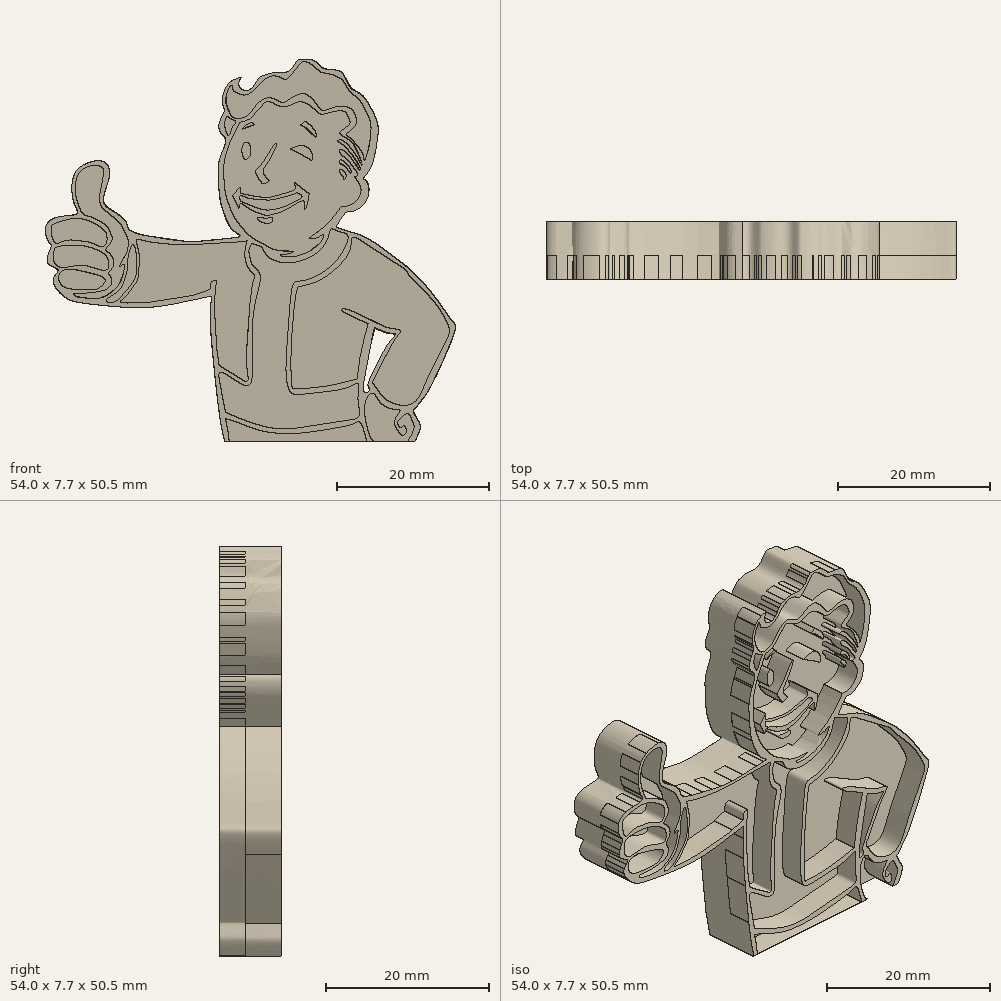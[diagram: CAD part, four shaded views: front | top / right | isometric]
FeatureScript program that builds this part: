
annotation { "Feature Type Name" : "Feature", "Feature Type Description" : "" }
export const myFeature = defineFeature(function(context is Context, id is Id, definition is map)
    precondition{}
    {
        {
            var Q0;
            Q0=qCreatedBy(makeId("Front.planeOp"),FACE);
            var sketch = newSketch(context, id + "F0", { "sketchPlane" : qUnion([Q0])});
            skPoint(sketch, "E0.middle", {"position": v(0.06, -0.1) * mm});
            skFitSpline(sketch, "E1", {"points": [v(-9.7, 22.56) * mm, v(-10.04, 21.79) * mm, v(-9.82, 21.14) * mm, v(-8.92, 20.8) * mm, v(-8.11, 21.32) * mm, v(-7.34, 22.43) * mm, v(-6.7, 22.81) * mm, v(-5.37, 23.16) * mm, v(-4.26, 23.16) * mm, v(-3.5, 23.33) * mm, v(-2.85, 23.97) * mm, v(-2.12, 24.87) * mm, v(-1.35, 24.95) * mm, v(-0.37, 24.87) * mm, v(0.57, 24.18) * mm, v(1.22, 23.71) * mm, v(3.01, 23.45) * mm, v(3.87, 22.73) * mm, v(4.77, 21.1) * mm, v(6, 20.37) * mm, v(7.3, 18.66) * mm, v(8.27, 16.35) * mm, v(8.19, 14.04) * mm, v(7.46, 10.84) * mm, v(6.38, 9.19) * mm], "startDerivative": vector(-13.84, -23.05) * mm, "endDerivative": vector(-23.15, -28.05) * mm});
            skFitSpline(sketch, "E2", {"points": [v(6.38, 9.19) * mm, v(7, 8.5) * mm, v(6.7, 6.13) * mm, v(4.94, 4.87) * mm, v(4.26, 4.8) * mm, v(2.75, 2.75) * mm], "startDerivative": vector(4.77, -3.33) * mm, "endDerivative": vector(-6.57, -11.06) * mm});
            skFitSpline(sketch, "E3", {"points": [v(2.75, 2.75) * mm, v(4.35, 2.21) * mm, v(6.38, 1.52) * mm, v(9.04, -0.1) * mm, v(11.12, -1.69) * mm, v(12.82, -3.08) * mm, v(14.78, -5.17) * mm, v(16.69, -7.65) * mm, v(18.02, -9.55) * mm, v(18.5, -10.25) * mm, v(17.75, -12.91) * mm], "startDerivative": vector(18.26, -6.4) * mm, "endDerivative": vector(-11.57, -29.08) * mm});
            skFitSpline(sketch, "E4", {"points": [v(17.75, -12.91) * mm, v(16.89, -14.9) * mm, v(14.98, -18.8) * mm, v(12.95, -21.49) * mm], "startDerivative": vector(-2.83, -6.5) * mm, "endDerivative": vector(-6.08, -7.14) * mm});
            skFitSpline(sketch, "E5", {"points": [v(12.95, -21.49) * mm, v(13.68, -22.87) * mm, v(13.9, -23.6) * mm, v(13.2, -25.5) * mm], "startDerivative": vector(2.25, -4.32) * mm, "endDerivative": vector(-2.57, -5.35) * mm});
            skLineSegment(sketch, "E6", {"start": v(13.2, -25.5) * mm, "end": v(6.78, -25.5) * mm});
            skFitSpline(sketch, "E7", {"points": [v(6.78, -25.5) * mm, v(6.33, -24.3) * mm, v(6.03, -23) * mm, v(6.15, -20.61) * mm, v(7.18, -18.83) * mm, v(7, -18.1) * mm, v(8, -15.77) * mm, v(9.55, -12.84) * mm, v(10.6, -11.37) * mm, v(9.94, -11.24) * mm, v(7.9, -10.53) * mm], "startDerivative": vector(-5.69, 14.05) * mm, "endDerivative": vector(-19.4, 8.58) * mm});
            skFitSpline(sketch, "E8", {"points": [v(7.9, -10.53) * mm, v(7.53, -12.15) * mm, v(6.78, -15.3) * mm, v(6.53, -19.02) * mm, v(7.18, -18.83) * mm], "startDerivative": vector(-1.55, -7.03) * mm, "endDerivative": vector(5.44, 3.45) * mm});
            skLineSegment(sketch, "E9", {"start": v(6.78, -25.5) * mm, "end": v(-11.9, -25.5) * mm});
            skFitSpline(sketch, "E10", {"points": [v(-11.9, -25.5) * mm, v(-12.56, -22.2) * mm, v(-13.1, -17.3) * mm, v(-13.7, -11.3) * mm, v(-13.67, -6.3) * mm], "startDerivative": vector(-3.46, 15) * mm, "endDerivative": vector(0.78, 19.03) * mm});
            skFitSpline(sketch, "E11", {"points": [v(-13.67, -6.3) * mm, v(-15.65, -6.7) * mm, v(-20.49, -7.64) * mm, v(-24.77, -7.77) * mm, v(-28.83, -7.42) * mm, v(-32.08, -6.87) * mm, v(-33.62, -5.84) * mm, v(-34.48, -4.05) * mm, v(-33.84, -2.9) * mm, v(-35.12, -2.03) * mm, v(-34.65, 0.4) * mm], "startDerivative": vector(-19.96, -3.7) * mm, "endDerivative": vector(14.11, 33.33) * mm});
            skFitSpline(sketch, "E12", {"points": [v(-34.65, 0.4) * mm, v(-35.3, 1.22) * mm, v(-35.38, 3.06) * mm, v(-33.92, 4.13) * mm, v(-31.65, 4.43) * mm, v(-31.27, 4.68) * mm, v(-31.65, 5.7) * mm, v(-32.04, 7.85) * mm, v(-31.44, 10.16) * mm, v(-29.39, 11.44) * mm, v(-27.63, 11.31) * mm, v(-27.03, 9.77) * mm, v(-27.55, 7.93) * mm, v(-27.8, 6) * mm, v(-26.78, 5.02) * mm, v(-24.94, 3.57) * mm, v(-24.42, 2.46) * mm, v(-20.45, 1.39) * mm, v(-15.82, 0.92) * mm, v(-10.82, 1.39) * mm, v(-9.75, 1.6) * mm, v(-10.82, 2.42) * mm, v(-12.1, 4.9) * mm, v(-12.53, 6.56) * mm, v(-12.74, 9.26) * mm, v(-12.53, 11.87) * mm, v(-11.76, 14.35) * mm, v(-12.49, 15.34) * mm, v(-12.53, 16.75) * mm, v(-11.93, 18.12) * mm, v(-12.15, 18.89) * mm, v(-12.1, 20.26) * mm, v(-11.18, 21.89) * mm, v(-9.7, 22.56) * mm], "startDerivative": vector(-31.91, 29.31) * mm, "endDerivative": vector(57.09, 16.2) * mm});
            skSolve(sketch);
        }
        {
            var Q0;
            Q0=makeQuery(id+"F0.imprint","IMPRINT",FACE,{"disambiguationData":[TD([[makeQuery(id+"F0.imprint","IMPRINT",EDGE,{"derivedFrom":sQuery(id+"F0.wireOp",EDGE,"E1")}),-1.0]])]});
            extrude(context, id + "F1", {"entities" : qUnion([Q0]), "depth" : 12.7 * mm});
        }
        {
            var Q0;
            Q0=makeQuery(id+"F1.opExtrude","CAP_FACE",FACE,{"disambiguationData":[OSD([sQuery(id+"F0.wireOp",EDGE,"E1"),sQuery(id+"F0.wireOp",EDGE,"E2"),sQuery(id+"F0.wireOp",EDGE,"E3"),sQuery(id+"F0.wireOp",EDGE,"E4"),sQuery(id+"F0.wireOp",EDGE,"E5"),sQuery(id+"F0.wireOp",EDGE,"E6"),sQuery(id+"F0.wireOp",EDGE,"E7"),sQuery(id+"F0.wireOp",EDGE,"E8"),sQuery(id+"F0.wireOp",EDGE,"E9"),sQuery(id+"F0.wireOp",EDGE,"E10"),sQuery(id+"F0.wireOp",EDGE,"E11"),sQuery(id+"F0.wireOp",EDGE,"E12")])],"isStart":false});
            var sketch = newSketch(context, id + "F2", { "sketchPlane" : qUnion([Q0])});
            skFitSpline(sketch, "E13", {"points": [v(-9.77, 1.56) * mm, v(-9.06, 1.13) * mm, v(-8.33, 0.7) * mm, v(-7.43, 0.36) * mm, v(-7.03, 0.19) * mm, v(-6.37, -0.92) * mm, v(-5.34, -1.57) * mm, v(-4, -1.89) * mm, v(-2.13, -1.72) * mm, v(-0.3, -0.99) * mm, v(0.9, 0) * mm, v(1.72, 1.36) * mm, v(2.2, 2.65) * mm, v(2.75, 2.75) * mm], "startDerivative": vector(11.12, -6.66) * mm, "endDerivative": vector(11.6, -0.98) * mm});
            skFitSpline(sketch, "E14", {"points": [v(-9.77, 1.56) * mm, v(-11.05, 2.67) * mm, v(-12.22, 5.26) * mm, v(-12.45, 6.12) * mm, v(-12.69, 8.2) * mm, v(-12.76, 10.65) * mm, v(-12.18, 12.77) * mm, v(-11.75, 14.25) * mm, v(-12.2, 14.99) * mm, v(-12.5, 15.37) * mm, v(-12.66, 15.93) * mm, v(-12.54, 16.72) * mm, v(-12, 17.84) * mm, v(-11.94, 18.27) * mm, v(-12.15, 18.91) * mm, v(-12.2, 19.7) * mm, v(-11.64, 21.33) * mm, v(-10.55, 22.27) * mm, v(-9.7, 22.56) * mm, v(-10.03, 21.83) * mm, v(-9.7, 21.03) * mm, v(-8.8, 20.82) * mm, v(-8.16, 21.26) * mm, v(-7.83, 21.71) * mm, v(-7.6, 22.08) * mm, v(-7.2, 22.56) * mm, v(-6.51, 22.88) * mm, v(-5.33, 23.16) * mm, v(-4.5, 23.16) * mm, v(-3.8, 23.2) * mm, v(-3.09, 23.66) * mm, v(-2.63, 24.3) * mm, v(-1.95, 24.93) * mm, v(-0.4, 24.88) * mm, v(0.39, 24.37) * mm, v(1.14, 23.74) * mm, v(2.32, 23.57) * mm, v(3.35, 23.31) * mm, v(3.96, 22.56) * mm, v(4.58, 21.32) * mm, v(5.66, 20.58) * mm, v(6.6, 19.76) * mm, v(7.4, 18.48) * mm, v(8.15, 16.84) * mm, v(8.33, 15.24) * mm, v(8.16, 13.82) * mm, v(8.02, 12.98) * mm, v(7.69, 11.5) * mm, v(7.2, 10.32) * mm, v(6.38, 9.19) * mm], "startDerivative": vector(-52.64, 32.33) * mm, "endDerivative": vector(-38.83, -49.05) * mm});
            skFitSpline(sketch, "E15", {"points": [v(6.38, 9.19) * mm, v(6.69, 8.95) * mm, v(7.05, 8.33) * mm, v(7.11, 7.93) * mm, v(7.12, 7.73) * mm, v(7.07, 7.12) * mm, v(7.03, 6.95) * mm, v(6.77, 6.23) * mm, v(6.26, 5.59) * mm, v(6.12, 5.46) * mm, v(5.4, 5) * mm, v(4.94, 4.87) * mm, v(4.65, 4.86) * mm, v(4.31, 4.82) * mm, v(3.95, 4.55) * mm, v(3.39, 3.8) * mm, v(2.75, 2.75) * mm], "startDerivative": vector(5.52, -3.35) * mm, "endDerivative": vector(-6.55, -11.06) * mm});
            skFitSpline(sketch, "E16", {"points": [v(-10.44, 17.13) * mm, v(-10.96, 17.45) * mm, v(-11.34, 18.04) * mm, v(-11.6, 18.7) * mm, v(-11.75, 19.8) * mm, v(-11.23, 21.23) * mm, v(-10.93, 21.52) * mm, v(-10.8, 20.94) * mm, v(-10.28, 20.5) * mm, v(-9.53, 20.24) * mm, v(-8.82, 20.3) * mm, v(-7.94, 20.85) * mm, v(-7.5, 21.35) * mm, v(-6.65, 22.2) * mm, v(-6.05, 22.56) * mm, v(-5.44, 22.74) * mm, v(-4.61, 22.56) * mm, v(-3.9, 22.25) * mm, v(-3.43, 22.56) * mm, v(-2.62, 23.44) * mm, v(-1.72, 24.54) * mm, v(-1.27, 24.6) * mm, v(-0.48, 24.27) * mm, v(0.44, 23.48) * mm, v(1.04, 23.15) * mm, v(2.28, 22.92) * mm, v(3.07, 22.56) * mm, v(3.66, 22.1) * mm, v(4.54, 20.76) * mm, v(5.26, 20.13) * mm, v(6.04, 19.32) * mm, v(7.03, 17.43) * mm, v(7.35, 16.35) * mm, v(7.37, 15.24) * mm, v(7.06, 13.08) * mm, v(6.52, 11.55) * mm, v(6.38, 12.2) * mm, v(5.59, 13.53) * mm, v(4.65, 14.54) * mm, v(4.17, 14.99) * mm, v(4.56, 15.37) * mm, v(5.44, 16.48) * mm, v(5.2, 17.85) * mm, v(4.9, 18.3) * mm, v(4.45, 18.58) * mm, v(3.54, 18.75) * mm, v(2.13, 18.46) * mm, v(1.07, 18.17) * mm, v(0.4, 18.73) * mm, v(-0.3, 19.66) * mm, v(-0.89, 20.13) * mm, v(-1.41, 20.38) * mm, v(-2.69, 20.06) * mm, v(-4.13, 19.23) * mm, v(-4.81, 19.41) * mm, v(-5.44, 19.74) * mm, v(-5.94, 19.86) * mm, v(-6.52, 19.74) * mm, v(-7.63, 18.96) * mm, v(-8.52, 17.81) * mm, v(-9.12, 17.34) * mm, v(-9.96, 17.07) * mm, v(-10.44, 17.13) * mm]});
            skFitSpline(sketch, "E17", {"points": [v(-11.5, 17.38) * mm, v(-11.18, 17.14) * mm, v(-10.42, 16.69) * mm, v(-10.6, 16.34) * mm, v(-10.95, 15.74) * mm, v(-11.33, 14.88) * mm, v(-11.76, 15.54) * mm, v(-11.89, 16.52) * mm, v(-11.6, 17.3) * mm, v(-11.5, 17.38) * mm]});
            skFitSpline(sketch, "E18", {"points": [v(-8.5, 17.07) * mm, v(-7.8, 17.84) * mm, v(-6.96, 18.76) * mm, v(-6.39, 19.32) * mm, v(-5.69, 19.25) * mm, v(-4.91, 18.85) * mm, v(-3.98, 18.69) * mm, v(-2.93, 18.98) * mm, v(-2.24, 19.3) * mm, v(-1.33, 19.22) * mm, v(0, 18.27) * mm, v(0.62, 17.74) * mm, v(1.37, 17.73) * mm, v(2.8, 18.1) * mm, v(3.93, 18) * mm, v(4.38, 17.34) * mm, v(4.55, 16.34) * mm, v(3.3, 15.25) * mm, v(4.32, 14.43) * mm, v(5.56, 12.92) * mm, v(6.2, 10.95) * mm, v(5.39, 12.34) * mm, v(3.93, 14.05) * mm, v(3.36, 14.33) * mm, v(2.98, 14.14) * mm], "startDerivative": vector(16.7, 18.66) * mm, "endDerivative": vector(-11.22, -13.2) * mm});
            skFitSpline(sketch, "E19", {"points": [v(2.98, 14.14) * mm, v(3.72, 13.62) * mm, v(4.72, 12.55) * mm, v(5.45, 11.57) * mm, v(5.94, 10.63) * mm, v(5.99, 10.22) * mm, v(5.7, 10.54) * mm, v(4.9, 11.76) * mm, v(3.63, 13) * mm, v(3.2, 13) * mm, v(3.42, 12.44) * mm, v(4.21, 11.76) * mm, v(5.13, 10.63) * mm, v(5.67, 9.66) * mm, v(5.22, 9.43) * mm], "startDerivative": vector(9.68, -6.14) * mm, "endDerivative": vector(-11.73, -2.82) * mm});
            skFitSpline(sketch, "E20", {"points": [v(5.22, 9.43) * mm, v(5.76, 8.62) * mm, v(6.07, 7.6) * mm, v(5.75, 6.58) * mm, v(5.22, 6.01) * mm, v(4.38, 5.6) * mm, v(3.5, 5.55) * mm], "startDerivative": vector(3.4, -4.56) * mm, "endDerivative": vector(-5.47, 0.19) * mm});
            skFitSpline(sketch, "E21", {"points": [v(3.5, 5.55) * mm, v(2.9, 4.68) * mm, v(1.92, 3.52) * mm, v(0.36, 2.12) * mm, v(-0.7, 1.32) * mm, v(-0.2, 1.3) * mm, v(0.69, 1.58) * mm, v(1.13, 1.83) * mm, v(1.07, 1.33) * mm, v(0.42, 0.41) * mm, v(-1.03, -0.55) * mm, v(-2.99, -1.09) * mm, v(-4.45, -0.97) * mm, v(-4.49, -0.82) * mm, v(-3.93, -0.78) * mm, v(-2.92, -0.53) * mm, v(-2.66, -0.36) * mm, v(-3.4, -0.36) * mm, v(-5.37, -0.13) * mm, v(-6.38, 0.36) * mm, v(-7.95, 1.2) * mm, v(-9.16, 2.22) * mm, v(-10.72, 4.3) * mm, v(-11.38, 5.87) * mm, v(-11.8, 7.24) * mm, v(-12.02, 10.53) * mm, v(-11.81, 12.04) * mm, v(-11.11, 14.11) * mm, v(-10.46, 15.38) * mm, v(-9.9, 16.53) * mm, v(-9.36, 16.74) * mm, v(-8.5, 17.07) * mm], "startDerivative": vector(-18.48, -28.57) * mm, "endDerivative": vector(32.44, 14.04) * mm});
            skLineSegment(sketch, "E22", {"start": v(-1.89, 16.24) * mm, "end": v(-1.29, 16.73) * mm});
            skPoint(sketch, "E23.4.internal.orphan", {"position": v(0, 14.81) * mm});
            skFitSpline(sketch, "E24", {"points": [v(-1.89, 16.24) * mm, v(-1.57, 16.1) * mm, v(-0.73, 15.53) * mm, v(0.17, 14.6) * mm, v(0.22, 14.89) * mm, v(-0.1, 15.63) * mm, v(-0.81, 16.42) * mm, v(-1.29, 16.73) * mm], "startDerivative": vector(2.93, -1.26) * mm, "endDerivative": vector(-3.57, 2.08) * mm});
            skLineSegment(sketch, "E25", {"start": v(-8.35, 16.62) * mm, "end": v(-8, 16.25) * mm});
            skFitSpline(sketch, "E26", {"points": [v(-8.35, 16.62) * mm, v(-9.26, 16.09) * mm, v(-9.58, 15.68) * mm, v(-9.14, 15.9) * mm, v(-8.35, 16.16) * mm, v(-8, 16.25) * mm], "startDerivative": vector(-3.72, -1.7) * mm, "endDerivative": vector(2.1, 0.55) * mm});
            skEllipse(sketch, "E27", {"center": v(-9.04, 12.85) * mm, "majorRadius": 1.13 * mm, "minorRadius": 0.6 * mm, "majorAxis": v(0, -1)});
            skFitSpline(sketch, "E28", {"points": [v(-3.24, 13.1) * mm, v(-1.9, 13.54) * mm, v(-1.08, 13.38) * mm, v(-0.54, 12.87) * mm, v(-0.27, 11.85) * mm, v(-0.36, 11.54) * mm], "startDerivative": vector(5.35, 2.3) * mm, "endDerivative": vector(-1.02, -1.98) * mm});
            skFitSpline(sketch, "E29", {"points": [v(-3.24, 13.1) * mm, v(-2.12, 12.57) * mm, v(-0.36, 11.54) * mm], "startDerivative": vector(2.42, -1.1) * mm, "endDerivative": vector(3.3, -2) * mm});
            skFitSpline(sketch, "E30", {"points": [v(-7.89, 10.1) * mm, v(-6.76, 11.44) * mm, v(-5.56, 13.35) * mm, v(-5.1, 13.8) * mm], "startDerivative": vector(3.08, 3.23) * mm, "endDerivative": vector(1.9, 1.51) * mm});
            skFitSpline(sketch, "E31", {"points": [v(-5.1, 13.8) * mm, v(-5.1, 13.46) * mm, v(-5.53, 12.49) * mm, v(-6.23, 11.2) * mm, v(-6.79, 10.37) * mm, v(-6.8, 10.04) * mm, v(-6.5, 9.45) * mm, v(-6.04, 8.86) * mm, v(-6.62, 8.57) * mm, v(-6.84, 8.57) * mm, v(-6.93, 8.55) * mm], "startDerivative": vector(0.57, -3.94) * mm, "endDerivative": vector(-2.22, -0.5) * mm});
            skFitSpline(sketch, "E32", {"points": [v(-7.89, 10.1) * mm, v(-7.36, 9.12) * mm, v(-6.93, 8.55) * mm], "startDerivative": vector(0.94, -1.9) * mm, "endDerivative": vector(0.98, -1.16) * mm});
            skFitSpline(sketch, "E33", {"points": [v(3.42, 11.68) * mm, v(3.3, 11.57) * mm, v(3.2, 11.3) * mm, v(3.76, 11) * mm, v(4.23, 10.52) * mm, v(4.74, 9.85) * mm, v(4.78, 10.1) * mm, v(4.3, 11) * mm, v(3.42, 11.68) * mm]});
            skFitSpline(sketch, "E34", {"points": [v(3.34, 10.38) * mm, v(3.51, 10.4) * mm, v(3.78, 10.16) * mm, v(4.12, 9.67) * mm, v(3.92, 9.1) * mm, v(3.8, 9.15) * mm, v(3.76, 9.34) * mm, v(3.49, 9.7) * mm, v(3.27, 9.99) * mm, v(3.21, 10.16) * mm, v(3.34, 10.38) * mm]});
            skFitSpline(sketch, "E35", {"points": [v(-0.75, 7.2) * mm, v(-2.8, 8.78) * mm], "startDerivative": vector(-2.06, 1.58) * mm, "endDerivative": vector(-2.06, 1.58) * mm});
            skPoint(sketch, "E36.10.internal.orphan", {"position": v(-9.7, 5.87) * mm});
            skFitSpline(sketch, "E37", {"points": [v(-2.8, 8.78) * mm, v(-2.58, 7.9) * mm, v(-2.8, 7.61) * mm, v(-4.51, 7.11) * mm, v(-5.75, 6.78) * mm, v(-7.69, 6.84) * mm, v(-9.8, 7.28) * mm], "startDerivative": vector(2.7, -7.29) * mm, "endDerivative": vector(-9.78, 2.36) * mm});
            skLineSegment(sketch, "E38", {"start": v(-9.8, 7.28) * mm, "end": v(-9.8, 8.1) * mm});
            skLineSegment(sketch, "E39", {"start": v(-9.8, 8.1) * mm, "end": v(-10.85, 6.95) * mm});
            skLineSegment(sketch, "E40", {"start": v(-10.85, 6.95) * mm, "end": v(-10, 5.3) * mm});
            skLineSegment(sketch, "E41", {"start": v(-10, 5.3) * mm, "end": v(-9.85, 5.9) * mm});
            skFitSpline(sketch, "E42", {"points": [v(-9.85, 5.9) * mm, v(-9.68, 5.9) * mm, v(-8.31, 5.04) * mm, v(-6.9, 4.5) * mm, v(-6.26, 4.36) * mm, v(-5, 4.63) * mm, v(-3.77, 5.12) * mm, v(-2, 6.13) * mm, v(-1.76, 6.24) * mm, v(-1.42, 6.18) * mm, v(-1.33, 5.1) * mm, v(-1.11, 5.47) * mm, v(-0.75, 7.2) * mm], "startDerivative": vector(3.8, 1.15) * mm, "endDerivative": vector(2.5, 16.43) * mm});
            skFitSpline(sketch, "E43", {"points": [v(-2.37, 7.32) * mm, v(-1.7, 6.87) * mm, v(-2.23, 6.36) * mm, v(-4.84, 5.24) * mm, v(-7.13, 5.18) * mm, v(-8.76, 5.82) * mm, v(-9.85, 6.35) * mm, v(-9.93, 6.83) * mm, v(-9.73, 6.98) * mm, v(-8.83, 6.64) * mm, v(-6.8, 6.43) * mm, v(-6.14, 6.37) * mm, v(-4.74, 6.59) * mm, v(-2.69, 7.2) * mm, v(-2.37, 7.32) * mm]});
            skFitSpline(sketch, "E44", {"points": [v(-7.56, 3.99) * mm, v(-6.26, 4) * mm, v(-5.68, 4.04) * mm, v(-5.58, 3.56) * mm, v(-6.08, 3.33) * mm, v(-7.16, 3.53) * mm, v(-7.56, 3.99) * mm]});
            skSolve(sketch);
        }
        {
            var Q0;
            {var subQ65=sQuery(id+"F2.wireOp",EDGE,"E13");Q0=makeQuery(id+"F2.imprint","IMPRINT",FACE,{"disambiguationData":[TD([[makeQuery(id+"F2.imprint","IMPRINT",EDGE,{"derivedFrom":subQ65}),1.0]])]});}
            var Q1;
            Q1=makeQuery(id+"F2.imprint","IMPRINT",FACE,{"disambiguationData":[TD([[makeQuery(id+"F2.imprint","IMPRINT",EDGE,{"derivedFrom":sQuery(id+"F2.wireOp",EDGE,"E27")}),1.0]])]});
            var Q2;
            Q2=makeQuery(id+"F2.imprint","IMPRINT",FACE,{"disambiguationData":[TD([[makeQuery(id+"F2.imprint","IMPRINT",EDGE,{"derivedFrom":sQuery(id+"F2.wireOp",EDGE,"E30")}),-1.0]])]});
            var Q3;
            Q3=makeQuery(id+"F2.imprint","IMPRINT",FACE,{"disambiguationData":[TD([[makeQuery(id+"F2.imprint","IMPRINT",EDGE,{"derivedFrom":sQuery(id+"F2.wireOp",EDGE,"E28")}),-1.0]])]});
            var Q4;
            Q4=makeQuery(id+"F2.imprint","IMPRINT",FACE,{"disambiguationData":[TD([[makeQuery(id+"F2.imprint","IMPRINT",EDGE,{"derivedFrom":sQuery(id+"F2.wireOp",EDGE,"E22")}),-1.0]])]});
            var Q5;
            Q5=makeQuery(id+"F2.imprint","IMPRINT",FACE,{"disambiguationData":[TD([[makeQuery(id+"F2.imprint","IMPRINT",EDGE,{"derivedFrom":sQuery(id+"F2.wireOp",EDGE,"E25")}),-1.0]])]});
            var Q6;
            Q6=makeQuery(id+"F2.imprint","IMPRINT",FACE,{"disambiguationData":[TD([[makeQuery(id+"F2.imprint","IMPRINT",EDGE,{"derivedFrom":sQuery(id+"F2.wireOp",EDGE,"E34")}),-1.0]])]});
            var Q7;
            Q7=makeQuery(id+"F2.imprint","IMPRINT",FACE,{"disambiguationData":[TD([[makeQuery(id+"F2.imprint","IMPRINT",EDGE,{"derivedFrom":sQuery(id+"F2.wireOp",EDGE,"E33")}),1.0]])]});
            var Q8;
            Q8=makeQuery(id+"F2.imprint","IMPRINT",FACE,{"disambiguationData":[TD([[makeQuery(id+"F2.imprint","IMPRINT",EDGE,{"derivedFrom":sQuery(id+"F2.wireOp",EDGE,"E35")}),1.0]])]});
            var Q9;
            Q9=makeQuery(id+"F2.imprint","IMPRINT",FACE,{"disambiguationData":[TD([[makeQuery(id+"F2.imprint","IMPRINT",EDGE,{"derivedFrom":sQuery(id+"F2.wireOp",EDGE,"E44")}),-1.0]])]});
            extrude(context, id + "F3", {"entities" : qUnion([Q0, Q1, Q2, Q3, Q4, Q5, Q6, Q7, Q8, Q9]), "operationType" : NewBodyOperationType.ADD, "depth" : 3.17 * mm});
        }
        {
            var Q0;
            {var subQ1=sQuery(id+"F0.wireOp",EDGE,"E2");var subQ4=sQuery(id+"F0.wireOp",EDGE,"E12");var subQ9=sQuery(id+"F0.wireOp",EDGE,"E3");var subQ11=sQuery(id+"F0.wireOp",EDGE,"E1");var subQ13=sQuery(id+"F0.wireOp",EDGE,"E5");var subQ14=sQuery(id+"F0.wireOp",EDGE,"E4");var subQ15=sQuery(id+"F0.wireOp",EDGE,"E9");var subQ16=sQuery(id+"F0.wireOp",EDGE,"E6");var subQ17=sQuery(id+"F0.wireOp",EDGE,"E7");var subQ19=sQuery(id+"F0.wireOp",EDGE,"E8");var subQ20=sQuery(id+"F0.wireOp",EDGE,"E10");var subQ21=sQuery(id+"F0.wireOp",EDGE,"E11");Q0=makeQuery(id+"F3.boolean.opBoolean","SPLIT",FACE,{"disambiguationData":[TD([makeQuery(id+"F1.opExtrude","SWEPT_FACE",FACE,{"disambiguationData":[OSD([subQ9])]})])],"derivedFrom":makeQuery(id+"F1.opExtrude","CAP_FACE",FACE,{"disambiguationData":[OSD([subQ11,subQ1,subQ9,subQ14,subQ13,subQ16,subQ17,subQ19,subQ15,subQ20,subQ21,subQ4])],"isStart":false})});}
            var sketch = newSketch(context, id + "F4", { "sketchPlane" : qUnion([Q0])});
            skFitSpline(sketch, "E45", {"points": [v(-9.54, 1.74) * mm, v(-9.77, 1.56) * mm, v(-11.43, 1.32) * mm, v(-13.74, 1.05) * mm, v(-15.6, 0.92) * mm, v(-17.6, 1) * mm, v(-19.14, 1.19) * mm, v(-20.71, 1.43) * mm, v(-22.58, 1.75) * mm, v(-24.03, 2.2) * mm, v(-24.56, 2.63) * mm, v(-24.9, 3.49) * mm, v(-25.28, 3.98) * mm, v(-25.95, 4.5) * mm, v(-26.5, 4.86) * mm, v(-27.72, 5.82) * mm, v(-27.84, 6.74) * mm, v(-27.65, 7.61) * mm, v(-27.36, 8.44) * mm, v(-27.04, 10.02) * mm, v(-27.34, 11) * mm, v(-27.75, 11.4) * mm, v(-28.5, 11.57) * mm, v(-30.57, 10.94) * mm, v(-31.52, 10.04) * mm, v(-32, 8.5) * mm, v(-32, 7.07) * mm, v(-31.52, 5.41) * mm, v(-31.27, 4.78) * mm, v(-31.66, 4.43) * mm, v(-32.77, 4.3) * mm, v(-34.14, 4.06) * mm, v(-35.43, 2.9) * mm, v(-35.41, 1.56) * mm, v(-35.06, 0.83) * mm, v(-34.65, 0.4) * mm], "startDerivative": vector(-10.92, -13.87) * mm, "endDerivative": vector(21.16, -19.27) * mm});
            skFitSpline(sketch, "E46", {"points": [v(-34.65, 0.4) * mm, v(-34.87, -0.1) * mm, v(-35.17, -0.9) * mm, v(-35.3, -1.55) * mm, v(-35.02, -2.13) * mm, v(-34.2, -2.59) * mm, v(-33.86, -2.84) * mm, v(-34.06, -3.37) * mm, v(-34.43, -3.9) * mm, v(-34.48, -4.5) * mm, v(-34.03, -5.37) * mm, v(-33.25, -6.2) * mm, v(-32.29, -6.8) * mm, v(-31.07, -7.13) * mm, v(-29.53, -7.35) * mm, v(-27.59, -7.55) * mm, v(-26.78, -7.62) * mm, v(-25.26, -7.74) * mm, v(-23.68, -7.8) * mm, v(-21.35, -7.73) * mm, v(-19.19, -7.44) * mm, v(-17.96, -7.2) * mm, v(-16.38, -6.86) * mm, v(-13.67, -6.3) * mm], "startDerivative": vector(-6.82, -15.77) * mm, "endDerivative": vector(46.31, 8.8) * mm});
            skFitSpline(sketch, "E47", {"points": [v(-12.65, -15.37) * mm, v(-11.9, -15.96) * mm, v(-10.1, -17.01) * mm, v(-8.9, -17.6) * mm, v(-8.99, -15.68) * mm, v(-8.99, -13.32) * mm, v(-8.45, -6.3) * mm, v(-8, -4) * mm, v(-7.93, -3.6) * mm, v(-8.48, -3.05) * mm, v(-9.22, -1.24) * mm, v(-9, 0.65) * mm, v(-8.88, 1.01) * mm], "startDerivative": vector(10.43, -9.19) * mm, "endDerivative": vector(2.96, 7.09) * mm});
            skFitSpline(sketch, "E48", {"points": [v(-13.67, -6.3) * mm, v(-13.73, -7.97) * mm, v(-13.73, -10.86) * mm, v(-13.38, -14.88) * mm, v(-12.78, -20.5) * mm, v(-11.9, -25.5) * mm], "startDerivative": vector(0.06, -11.63) * mm, "endDerivative": vector(3.97, -20.81) * mm});
            skFitSpline(sketch, "E49", {"points": [v(-12.65, -15.37) * mm, v(-12.94, -13.24) * mm, v(-13.23, -7.36) * mm, v(-12.98, -4.19) * mm], "startDerivative": vector(-1.13, 6.88) * mm, "endDerivative": vector(1.1, 8.84) * mm});
            skFitSpline(sketch, "E50", {"points": [v(-12.98, -4.19) * mm, v(-13.64, -4.48) * mm, v(-13.79, -5.4) * mm], "startDerivative": vector(-1.69, -0.36) * mm, "endDerivative": vector(0.03, -2.05) * mm});
            skFitSpline(sketch, "E51", {"points": [v(-13.79, -5.4) * mm, v(-15.62, -6.05) * mm, v(-15.65, -6.06) * mm], "startDerivative": vector(-2.86, -1) * mm, "endDerivative": vector(-0.17, -0.05) * mm});
            skFitSpline(sketch, "E52", {"points": [v(-15.62, -6.05) * mm, v(-16.03, -6.19) * mm, v(-19.91, -6.85) * mm, v(-21.95, -7.1) * mm, v(-25.63, -7.06) * mm, v(-25.22, -6.63) * mm, v(-23.87, -4.98) * mm, v(-23.33, -3.93) * mm, v(-23.2, -2.57) * mm, v(-23.06, -1.78) * mm, v(-23.46, 0.61) * mm, v(-23.55, 1.21) * mm, v(-22.9, 1.1) * mm, v(-20.3, 0.67) * mm, v(-16.27, 0.5) * mm, v(-13.16, 0.73) * mm, v(-8.88, 1.01) * mm, v(-8.63, 1.24) * mm, v(-9.54, 1.74) * mm], "startDerivative": vector(-9.45, -4.53) * mm, "endDerivative": vector(-29.5, 12.18) * mm});
            skFitSpline(sketch, "E53", {"points": [v(-28.1, 5.48) * mm, v(-28.37, 6.4) * mm, v(-28.27, 7.6) * mm, v(-27.9, 9.42) * mm, v(-27.86, 9.95) * mm, v(-27.97, 10.57) * mm, v(-28.55, 10.93) * mm, v(-29.66, 10.84) * mm, v(-30.98, 10.01) * mm, v(-31.6, 7.67) * mm, v(-31.04, 5.4) * mm, v(-30.5, 4.49) * mm, v(-29.53, 4.17) * mm, v(-28.5, 3.64) * mm, v(-27.47, 3.03) * mm, v(-26.97, 2.08) * mm, v(-26.76, 1.01) * mm, v(-27.54, -0.19) * mm, v(-27.28, -0.47) * mm, v(-26.59, -1.4) * mm, v(-26.64, -2.54) * mm, v(-27.16, -3.27) * mm, v(-26.9, -3.72) * mm, v(-26.83, -4.66) * mm, v(-27.5, -5.4) * mm, v(-30.95, -5.9) * mm, v(-31.88, -5.92) * mm, v(-31.69, -6.17) * mm, v(-30.99, -6.47) * mm, v(-30.85, -6.47) * mm, v(-29.5, -6.6) * mm, v(-27.71, -6.36) * mm, v(-25.89, -4.91) * mm, v(-25.19, -3.09) * mm, v(-25.2, -2.09) * mm, v(-25.73, -2.42) * mm, v(-25.42, -1.68) * mm, v(-24.91, -0.85) * mm, v(-24.62, 0.21) * mm, v(-24.66, 1.27) * mm, v(-25.05, 2.22) * mm, v(-25.62, 3.2) * mm, v(-26.48, 4.06) * mm, v(-27.59, 4.96) * mm, v(-28.1, 5.48) * mm]});
            skFitSpline(sketch, "E54", {"points": [v(-23.94, 0.5) * mm, v(-24.64, -1.28) * mm, v(-24.66, -2.47) * mm, v(-25.1, -4.19) * mm, v(-25.95, -5.66) * mm, v(-27.53, -6.9) * mm, v(-26.6, -7.12) * mm, v(-25.44, -6.3) * mm, v(-23.76, -4.06) * mm, v(-23.5, -2.78) * mm, v(-23.52, -1.09) * mm, v(-23.94, 0.5) * mm]});
            skFitSpline(sketch, "E55", {"points": [v(-34.43, 3.17) * mm, v(-34.76, 2.75) * mm, v(-34.65, 1.56) * mm, v(-34.09, 0.63) * mm, v(-32.98, 1.01) * mm, v(-30.9, 1.01) * mm, v(-29.37, 0.7) * mm, v(-28.13, 0.21) * mm, v(-27.53, 0.57) * mm, v(-27.47, 1.87) * mm, v(-28.05, 2.64) * mm, v(-29.9, 3.7) * mm, v(-32, 3.9) * mm, v(-34.43, 3.17) * mm]});
            skFitSpline(sketch, "E56", {"points": [v(-33.94, 0.2) * mm, v(-32.46, 0.43) * mm, v(-29.95, 0.24) * mm, v(-27.5, -1.01) * mm, v(-27.15, -2.15) * mm, v(-27.41, -2.84) * mm, v(-29.11, -2.57) * mm, v(-31.1, -2.22) * mm, v(-33.67, -2.46) * mm, v(-34.43, -1.47) * mm, v(-34.32, -0.18) * mm, v(-33.94, 0.2) * mm]});
            skFitSpline(sketch, "E57", {"points": [v(-32.2, -2.7) * mm, v(-33.4, -3.06) * mm, v(-33.75, -4.08) * mm, v(-33.3, -4.88) * mm, v(-32.46, -5.27) * mm, v(-31.09, -5.42) * mm, v(-28.93, -5.4) * mm, v(-28.15, -5.02) * mm, v(-27.61, -4.23) * mm, v(-28.73, -3.46) * mm, v(-31.39, -2.82) * mm, v(-32.2, -2.7) * mm]});
            skFitSpline(sketch, "E58", {"points": [v(-11.8, -21.59) * mm, v(-10.55, -22.22) * mm, v(-6.26, -23.63) * mm, v(-2.3, -23.75) * mm, v(4.39, -22.7) * mm, v(5.82, -22.24) * mm, v(5.67, -19.86) * mm, v(5.67, -17.85) * mm, v(4.64, -18.3) * mm, v(-0.85, -19.22) * mm, v(-3.03, -19.15) * mm, v(-3.7, -17.66) * mm, v(-3.77, -14) * mm, v(-3.43, -9.48) * mm, v(-2.9, -5) * mm, v(-2.38, -4.45) * mm, v(-1.44, -4.31) * mm, v(0.93, -3.34) * mm, v(3.49, -0.86) * mm, v(4.33, 1.63) * mm, v(3.47, 2.06) * mm, v(1.94, 2.67) * mm], "startDerivative": vector(28.8, -16.17) * mm, "endDerivative": vector(-40.93, 18.53) * mm});
            skFitSpline(sketch, "E59", {"points": [v(-11.8, -22.5) * mm, v(-11.46, -24.18) * mm, v(-11.28, -25.5) * mm], "startDerivative": vector(0.72, -3.24) * mm, "endDerivative": vector(0.3, -2.74) * mm});
            skFitSpline(sketch, "E60", {"points": [v(-11.8, -22.5) * mm, v(-10.25, -22.97) * mm, v(-6.78, -24.18) * mm, v(-1.75, -24.4) * mm, v(1.85, -23.9) * mm, v(5.2, -23.14) * mm, v(5.88, -22.92) * mm, v(6.85, -25.5) * mm], "startDerivative": vector(13.11, -3.37) * mm, "endDerivative": vector(6.55, -25.3) * mm});
            skFitSpline(sketch, "E61", {"points": [v(-2.27, -5.18) * mm, v(-2.58, -6.68) * mm, v(-3.18, -14.31) * mm, v(-3, -18.56) * mm], "startDerivative": vector(-1.49, -5.53) * mm, "endDerivative": vector(0.92, -10.73) * mm});
            skFitSpline(sketch, "E62", {"points": [v(-3, -18.56) * mm, v(-1.74, -18.56) * mm, v(1.44, -18.24) * mm, v(5.56, -17.3) * mm], "startDerivative": vector(4.97, -0.12) * mm, "endDerivative": vector(9.98, 2.58) * mm});
            skFitSpline(sketch, "E63", {"points": [v(5.56, -17.3) * mm, v(5.95, -14.4) * mm, v(7, -10.02) * mm], "startDerivative": vector(0.65, 6.2) * mm, "endDerivative": vector(2.2, 8.31) * mm});
            skFitSpline(sketch, "E64", {"points": [v(7, -10.02) * mm, v(3.54, -8.17) * mm, v(4.05, -8.07) * mm, v(8.39, -10.02) * mm, v(9.8, -10.56) * mm, v(11.25, -10.93) * mm, v(10.58, -12.08) * mm, v(8.07, -16.76) * mm, v(7.63, -17.73) * mm, v(7.97, -18.27) * mm, v(9.55, -20.1) * mm, v(12.8, -20.56) * mm, v(14.8, -17.3) * mm, v(17.58, -11.72) * mm, v(17.7, -10.53) * mm, v(16.71, -8.56) * mm, v(15.14, -6.44) * mm, v(12.23, -3.36) * mm, v(12.03, -3) * mm, v(7.28, 0.23) * mm, v(4.98, 1.3) * mm, v(4.71, 0) * mm, v(3.51, -2.06) * mm, v(0.64, -4.29) * mm, v(-2.27, -5.18) * mm], "startDerivative": vector(-97.45, 43.98) * mm, "endDerivative": vector(-63, -13.27) * mm});
            skFitSpline(sketch, "E65", {"points": [v(6.65, -19.07) * mm, v(6.43, -18.83) * mm, v(6.38, -18.2) * mm, v(7.33, -12.91) * mm, v(7.9, -10.53) * mm, v(8.08, -10.6) * mm, v(8.62, -10.84) * mm, v(9.3, -11.1) * mm, v(10.03, -11.25) * mm, v(10.55, -11.32) * mm, v(10.57, -11.5) * mm, v(10.04, -12.22) * mm, v(9.5, -12.91) * mm, v(8.6, -14.51) * mm, v(7.51, -16.69) * mm, v(7, -17.91) * mm, v(7, -18.19) * mm, v(7.18, -18.83) * mm, v(6.65, -19.07) * mm]});
            skFitSpline(sketch, "E66", {"points": [v(11.34, -21.4) * mm, v(9.93, -21.17) * mm, v(8.5, -20.24) * mm, v(7.6, -19.15) * mm, v(6.58, -20.73) * mm, v(7.37, -25.06) * mm, v(7.9, -25.5) * mm, v(12.27, -25.5) * mm], "startDerivative": vector(-11.8, 0.95) * mm, "endDerivative": vector(26.49, 0.97) * mm});
            skFitSpline(sketch, "E67", {"points": [v(11.34, -21.4) * mm, v(10.88, -22.06) * mm, v(10.5, -23.14) * mm, v(10.96, -24.15) * mm, v(11.49, -24.71) * mm, v(12.02, -24.43) * mm, v(11.74, -23.43) * mm, v(11.34, -23.7) * mm, v(10.92, -23.1) * mm, v(11.62, -22.2) * mm, v(12.28, -21.83) * mm, v(12.71, -22.54) * mm, v(13.07, -23.57) * mm, v(12.27, -25.5) * mm], "startDerivative": vector(-6.24, -8.5) * mm, "endDerivative": vector(-10.38, -18.2) * mm});
            skFitSpline(sketch, "E68", {"points": [v(12.27, -25.5) * mm, v(13.2, -25.5) * mm], "startDerivative": vector(0.92, 0) * mm, "endDerivative": vector(0.92, 0) * mm});
            skFitSpline(sketch, "E69", {"points": [v(13.2, -25.5) * mm, v(13.4, -25.08) * mm, v(13.79, -24.14) * mm, v(13.9, -23.59) * mm, v(13.89, -23.35) * mm, v(13.57, -22.66) * mm, v(12.95, -21.49) * mm, v(13.1, -21.32) * mm, v(13.56, -20.76) * mm, v(14.5, -19.54) * mm, v(15.12, -18.56) * mm, v(16.56, -15.64) * mm, v(17.59, -13.29) * mm, v(18.26, -11.57) * mm, v(18.5, -10.23) * mm, v(18.24, -9.79) * mm, v(17.93, -9.45) * mm, v(17.42, -8.75) * mm, v(16.77, -7.76) * mm, v(15.7, -6.3) * mm, v(15.07, -5.5) * mm, v(14.48, -4.8) * mm, v(13.2, -3.44) * mm, v(12.02, -2.4) * mm, v(11.34, -1.86) * mm, v(10.2, -0.97) * mm, v(9.15, -0.18) * mm, v(8.31, 0.4) * mm, v(6.76, 1.34) * mm, v(6.14, 1.63) * mm, v(5.99, 1.69) * mm, v(4.36, 2.2) * mm, v(3.13, 2.61) * mm, v(2.34, 2.88) * mm, v(1.94, 2.67) * mm], "startDerivative": vector(9.02, 18.61) * mm, "endDerivative": vector(-18.86, -14.93) * mm});
            skLineSegment(sketch, "E70", {"start": v(-11.9, -25.5) * mm, "end": v(-11.28, -25.5) * mm});
            skLineSegment(sketch, "E71", {"start": v(6.85, -25.5) * mm, "end": v(7.9, -25.5) * mm});
            skLineSegment(sketch, "E72", {"start": v(-13.67, -6.3) * mm, "end": v(-13.19, -6.3) * mm});
            skLineSegment(sketch, "E73", {"start": v(-13.38, -14.88) * mm, "end": v(-12.65, -15.37) * mm});
            skSolve(sketch);
        }
        {
            var Q0;
            {var subQ0=sQuery(id+"F4.wireOp",EDGE,"E72");Q0=makeQuery(id+"F4.imprint","IMPRINT",FACE,{"disambiguationData":[TD([[makeQuery(id+"F4.imprint","IMPRINT",EDGE,{"derivedFrom":subQ0}),-1.0]])]});}
            var Q1;
            {var subQ53=sQuery(id+"F4.wireOp",EDGE,"E50");Q1=makeQuery(id+"F4.imprint","IMPRINT",FACE,{"disambiguationData":[TD([[makeQuery(id+"F4.imprint","IMPRINT",EDGE,{"derivedFrom":subQ53}),1.0]])]});}
            extrude(context, id + "F5", {"entities" : qUnion([Q0, Q1]), "operationType" : NewBodyOperationType.ADD, "depth" : 3.17 * mm});
        }
        {
            var Q0;
            {var subQ1=sQuery(id+"F0.wireOp",EDGE,"E2");var subQ6=sQuery(id+"F0.wireOp",EDGE,"E3");var subQ7=makeQuery(id+"F1.opExtrude","SWEPT_FACE",FACE,{"disambiguationData":[OSD([subQ6])]});var subQ13=sQuery(id+"F0.wireOp",EDGE,"E1");var subQ16=sQuery(id+"F0.wireOp",EDGE,"E5");var subQ19=sQuery(id+"F0.wireOp",EDGE,"E12");var subQ30=sQuery(id+"F0.wireOp",EDGE,"E11");var subQ31=sQuery(id+"F0.wireOp",EDGE,"E10");var subQ32=sQuery(id+"F0.wireOp",EDGE,"E9");var subQ33=sQuery(id+"F0.wireOp",EDGE,"E8");var subQ34=sQuery(id+"F0.wireOp",EDGE,"E7");var subQ35=sQuery(id+"F0.wireOp",EDGE,"E6");var subQ36=sQuery(id+"F0.wireOp",EDGE,"E4");var subQ37=makeQuery(id+"F1.opExtrude","CAP_FACE",FACE,{"disambiguationData":[OSD([subQ13,subQ1,subQ6,subQ36,subQ16,subQ35,subQ34,subQ33,subQ32,subQ31,subQ30,subQ19])],"isStart":false});var subQ49=makeQuery(id+"F1.opExtrude","SWEPT_FACE",FACE,{"disambiguationData":[OSD([subQ1])]});Q0=makeQuery(id+"FRotD5eydtJjERD_1.boolean.opBoolean","SPLIT",FACE,{"disambiguationData":[TD([subQ49])],"derivedFrom":makeQuery(id+"F3.boolean.opBoolean","SPLIT",FACE,{"disambiguationData":[TD([subQ7])],"derivedFrom":subQ37})});}
            var sketch = newSketch(context, id + "F6", { "sketchPlane" : qUnion([Q0])});
            skFitSpline(sketch, "E74", {"points": [v(-9.55, 1.83) * mm, v(-9.78, 1.64) * mm, v(-11.44, 1.4) * mm, v(-13.75, 1.13) * mm, v(-15.6, 1) * mm, v(-17.61, 1.08) * mm, v(-19.15, 1.27) * mm, v(-20.72, 1.51) * mm, v(-22.59, 1.83) * mm, v(-24.04, 2.28) * mm, v(-24.57, 2.7) * mm, v(-24.9, 3.57) * mm, v(-25.29, 4.06) * mm, v(-25.96, 4.58) * mm, v(-26.51, 4.94) * mm, v(-27.73, 5.9) * mm, v(-27.85, 6.82) * mm, v(-27.66, 7.7) * mm, v(-27.37, 8.52) * mm, v(-27.05, 10.1) * mm, v(-27.35, 11.07) * mm, v(-27.76, 11.48) * mm, v(-28.5, 11.65) * mm, v(-30.58, 11.02) * mm, v(-31.53, 10.12) * mm, v(-32.02, 8.59) * mm, v(-32, 7.16) * mm, v(-31.53, 5.5) * mm, v(-31.28, 4.86) * mm, v(-31.66, 4.5) * mm, v(-32.78, 4.39) * mm, v(-34.14, 4.15) * mm, v(-35.43, 3) * mm, v(-35.42, 1.64) * mm, v(-35.06, 0.9) * mm, v(-34.66, 0.49) * mm], "startDerivative": vector(-10.92, -13.87) * mm, "endDerivative": vector(21.16, -19.27) * mm});
            skFitSpline(sketch, "E75", {"points": [v(-34.66, 0.49) * mm, v(-34.88, -0.03) * mm, v(-35.18, -0.81) * mm, v(-35.3, -1.47) * mm, v(-35.03, -2.05) * mm, v(-34.2, -2.5) * mm, v(-33.87, -2.76) * mm, v(-34.07, -3.3) * mm, v(-34.43, -3.82) * mm, v(-34.49, -4.43) * mm, v(-34.04, -5.29) * mm, v(-33.26, -6.11) * mm, v(-32.3, -6.7) * mm, v(-31.08, -7.05) * mm, v(-29.54, -7.27) * mm, v(-27.6, -7.47) * mm, v(-26.8, -7.54) * mm, v(-25.26, -7.66) * mm, v(-23.69, -7.72) * mm, v(-21.36, -7.65) * mm, v(-19.2, -7.35) * mm, v(-17.97, -7.12) * mm, v(-16.39, -6.77) * mm, v(-13.67, -6.22) * mm], "startDerivative": vector(-6.82, -15.77) * mm, "endDerivative": vector(46.31, 8.8) * mm});
            skFitSpline(sketch, "E76", {"points": [v(-12.65, -15.29) * mm, v(-11.9, -15.87) * mm, v(-10.1, -16.93) * mm, v(-8.9, -17.52) * mm, v(-9, -15.6) * mm, v(-9, -13.24) * mm, v(-8.45, -6.22) * mm, v(-8, -3.9) * mm, v(-7.94, -3.53) * mm, v(-8.48, -2.97) * mm, v(-9.23, -1.15) * mm, v(-9.01, 0.74) * mm, v(-8.88, 1.1) * mm], "startDerivative": vector(10.43, -9.19) * mm, "endDerivative": vector(2.96, 7.09) * mm});
            skFitSpline(sketch, "E77", {"points": [v(-13.67, -6.22) * mm, v(-13.74, -7.89) * mm, v(-13.74, -10.78) * mm, v(-13.39, -14.8) * mm, v(-12.78, -20.4) * mm, v(-11.9, -25.42) * mm], "startDerivative": vector(0.06, -11.63) * mm, "endDerivative": vector(3.97, -20.81) * mm});
            skFitSpline(sketch, "E78", {"points": [v(-12.99, -4.1) * mm, v(-13.65, -4.4) * mm, v(-13.8, -5.33) * mm], "startDerivative": vector(-1.69, -0.36) * mm, "endDerivative": vector(0.03, -2.05) * mm});
            skFitSpline(sketch, "E79", {"points": [v(-13.8, -5.33) * mm, v(-15.62, -5.96) * mm, v(-15.65, -5.97) * mm], "startDerivative": vector(-2.86, -1) * mm, "endDerivative": vector(-0.17, -0.05) * mm});
            skFitSpline(sketch, "E80", {"points": [v(-15.62, -5.96) * mm, v(-16.04, -6.1) * mm, v(-19.92, -6.76) * mm, v(-21.96, -7.01) * mm, v(-25.63, -6.98) * mm, v(-25.22, -6.54) * mm, v(-23.87, -4.9) * mm, v(-23.33, -3.85) * mm, v(-23.2, -2.49) * mm, v(-23.07, -1.7) * mm, v(-23.46, 0.7) * mm, v(-23.55, 1.3) * mm, v(-22.9, 1.2) * mm, v(-20.32, 0.75) * mm, v(-16.27, 0.58) * mm, v(-13.17, 0.8) * mm, v(-8.88, 1.1) * mm, v(-8.64, 1.32) * mm, v(-9.55, 1.83) * mm], "startDerivative": vector(-9.45, -4.53) * mm, "endDerivative": vector(-29.5, 12.18) * mm});
            skFitSpline(sketch, "E81", {"points": [v(-28.11, 5.57) * mm, v(-28.38, 6.49) * mm, v(-28.27, 7.68) * mm, v(-27.9, 9.5) * mm, v(-27.86, 10.03) * mm, v(-27.98, 10.65) * mm, v(-28.55, 11.02) * mm, v(-29.67, 10.93) * mm, v(-30.98, 10.1) * mm, v(-31.61, 7.75) * mm, v(-31.04, 5.48) * mm, v(-30.5, 4.57) * mm, v(-29.53, 4.25) * mm, v(-28.5, 3.73) * mm, v(-27.48, 3.12) * mm, v(-26.98, 2.16) * mm, v(-26.77, 1.1) * mm, v(-27.55, -0.1) * mm, v(-27.3, -0.38) * mm, v(-26.6, -1.32) * mm, v(-26.65, -2.46) * mm, v(-27.17, -3.19) * mm, v(-26.9, -3.64) * mm, v(-26.84, -4.58) * mm, v(-27.5, -5.33) * mm, v(-30.95, -5.82) * mm, v(-31.9, -5.83) * mm, v(-31.7, -6.09) * mm, v(-31, -6.4) * mm, v(-30.86, -6.4) * mm, v(-29.52, -6.52) * mm, v(-27.72, -6.28) * mm, v(-25.9, -4.83) * mm, v(-25.2, -3) * mm, v(-25.2, -2) * mm, v(-25.73, -2.34) * mm, v(-25.43, -1.6) * mm, v(-24.92, -0.76) * mm, v(-24.63, 0.3) * mm, v(-24.66, 1.36) * mm, v(-25.06, 2.3) * mm, v(-25.62, 3.29) * mm, v(-26.49, 4.14) * mm, v(-27.6, 5.04) * mm, v(-28.11, 5.57) * mm]});
            skFitSpline(sketch, "E82", {"points": [v(-23.95, 0.58) * mm, v(-24.64, -1.2) * mm, v(-24.66, -2.39) * mm, v(-25.1, -4.1) * mm, v(-25.96, -5.58) * mm, v(-27.54, -6.83) * mm, v(-26.62, -7.04) * mm, v(-25.45, -6.21) * mm, v(-23.77, -3.98) * mm, v(-23.5, -2.7) * mm, v(-23.53, -1) * mm, v(-23.95, 0.58) * mm]});
            skFitSpline(sketch, "E83", {"points": [v(-34.44, 3.26) * mm, v(-34.77, 2.83) * mm, v(-34.66, 1.64) * mm, v(-34.1, 0.7) * mm, v(-32.99, 1.1) * mm, v(-30.91, 1.1) * mm, v(-29.38, 0.8) * mm, v(-28.14, 0.3) * mm, v(-27.54, 0.66) * mm, v(-27.48, 1.95) * mm, v(-28.06, 2.73) * mm, v(-29.9, 3.77) * mm, v(-32.02, 4) * mm, v(-34.44, 3.26) * mm]});
            skFitSpline(sketch, "E84", {"points": [v(-33.95, 0.28) * mm, v(-32.47, 0.5) * mm, v(-29.96, 0.32) * mm, v(-27.5, -0.93) * mm, v(-27.16, -2.06) * mm, v(-27.42, -2.75) * mm, v(-29.12, -2.48) * mm, v(-31.1, -2.14) * mm, v(-33.68, -2.37) * mm, v(-34.44, -1.39) * mm, v(-34.33, -0.1) * mm, v(-33.95, 0.28) * mm]});
            skFitSpline(sketch, "E85", {"points": [v(-32.21, -2.62) * mm, v(-33.4, -2.98) * mm, v(-33.76, -4) * mm, v(-33.3, -4.8) * mm, v(-32.46, -5.2) * mm, v(-31.1, -5.34) * mm, v(-28.94, -5.31) * mm, v(-28.15, -4.94) * mm, v(-27.62, -4.15) * mm, v(-28.74, -3.38) * mm, v(-31.4, -2.74) * mm, v(-32.21, -2.62) * mm]});
            skFitSpline(sketch, "E86", {"points": [v(-11.8, -21.5) * mm, v(-12.37, -18.57) * mm, v(-12.5, -16.33) * mm, v(-10.15, -17.6) * mm, v(-8.62, -18.03) * mm, v(-8.29, -15.65) * mm, v(-8, -7.77) * mm, v(-7.2, -3.6) * mm, v(-7.84, -2.57) * mm, v(-8.31, -2.05) * mm, v(-8.58, -1.1) * mm, v(-8.71, -0.37) * mm, v(-8.7, -0.24) * mm, v(-8.29, 1.02) * mm, v(-8.64, 1.32) * mm], "startDerivative": vector(-5.18, 29.45) * mm, "endDerivative": vector(-13.47, 4.43) * mm});
            skFitSpline(sketch, "E87", {"points": [v(-11.8, -21.5) * mm, v(-10.55, -22.14) * mm, v(-6.27, -23.55) * mm, v(-2.31, -23.67) * mm, v(4.38, -22.61) * mm, v(5.8, -22.16) * mm, v(5.66, -19.78) * mm, v(5.66, -17.77) * mm, v(4.63, -18.22) * mm, v(-0.86, -19.13) * mm, v(-3.04, -19.07) * mm, v(-3.7, -17.58) * mm, v(-3.78, -13.91) * mm, v(-3.43, -9.4) * mm, v(-2.9, -4.9) * mm, v(-2.39, -4.37) * mm, v(-1.45, -4.23) * mm, v(0.92, -3.25) * mm, v(3.48, -0.78) * mm, v(4.32, 1.71) * mm, v(3.47, 2.15) * mm, v(1.93, 2.76) * mm], "startDerivative": vector(28.8, -16.17) * mm, "endDerivative": vector(-40.93, 18.53) * mm});
            skFitSpline(sketch, "E88", {"points": [v(-11.8, -22.42) * mm, v(-11.46, -24.1) * mm, v(-11.3, -25.42) * mm], "startDerivative": vector(0.72, -3.24) * mm, "endDerivative": vector(0.3, -2.74) * mm});
            skFitSpline(sketch, "E89", {"points": [v(-11.8, -22.42) * mm, v(-10.26, -22.89) * mm, v(-6.78, -24.1) * mm, v(-1.76, -24.32) * mm, v(1.84, -23.82) * mm, v(5.19, -23.06) * mm, v(5.88, -22.84) * mm, v(6.84, -25.42) * mm], "startDerivative": vector(13.11, -3.37) * mm, "endDerivative": vector(6.55, -25.3) * mm});
            skFitSpline(sketch, "E90", {"points": [v(-2.28, -5.1) * mm, v(-2.6, -6.6) * mm, v(-3.18, -14.23) * mm, v(-3, -18.48) * mm], "startDerivative": vector(-1.49, -5.53) * mm, "endDerivative": vector(0.92, -10.73) * mm});
            skFitSpline(sketch, "E91", {"points": [v(-3, -18.48) * mm, v(-1.74, -18.48) * mm, v(1.44, -18.16) * mm, v(5.55, -17.22) * mm], "startDerivative": vector(4.97, -0.12) * mm, "endDerivative": vector(9.98, 2.58) * mm});
            skFitSpline(sketch, "E92", {"points": [v(5.55, -17.22) * mm, v(5.94, -14.32) * mm, v(7, -9.93) * mm], "startDerivative": vector(0.65, 6.2) * mm, "endDerivative": vector(2.2, 8.31) * mm});
            skFitSpline(sketch, "E93", {"points": [v(7, -9.93) * mm, v(3.53, -8.09) * mm, v(4.05, -7.99) * mm, v(8.38, -9.93) * mm, v(9.79, -10.47) * mm, v(11.24, -10.84) * mm, v(10.57, -12) * mm, v(8.06, -16.68) * mm, v(7.62, -17.64) * mm, v(7.96, -18.19) * mm, v(9.54, -20) * mm, v(12.8, -20.48) * mm, v(14.79, -17.22) * mm, v(17.57, -11.63) * mm, v(17.7, -10.45) * mm, v(16.7, -8.48) * mm, v(15.13, -6.36) * mm, v(12.22, -3.28) * mm, v(12.03, -2.91) * mm, v(7.27, 0.31) * mm, v(4.97, 1.39) * mm, v(4.7, 0.08) * mm, v(3.5, -1.98) * mm, v(0.63, -4.2) * mm, v(-2.28, -5.1) * mm], "startDerivative": vector(-97.45, 43.98) * mm, "endDerivative": vector(-63, -13.27) * mm});
            skFitSpline(sketch, "E94", {"points": [v(6.64, -18.99) * mm, v(6.42, -18.75) * mm, v(6.38, -18.11) * mm, v(7.33, -12.83) * mm, v(7.9, -10.45) * mm, v(8.08, -10.53) * mm, v(8.61, -10.76) * mm, v(9.3, -11.01) * mm, v(10.02, -11.17) * mm, v(10.54, -11.23) * mm, v(10.56, -11.42) * mm, v(10.03, -12.14) * mm, v(9.5, -12.83) * mm, v(8.6, -14.43) * mm, v(7.5, -16.6) * mm, v(7, -17.83) * mm, v(7, -18.1) * mm, v(7.17, -18.75) * mm, v(6.64, -18.99) * mm]});
            skFitSpline(sketch, "E95", {"points": [v(11.33, -21.31) * mm, v(9.93, -21.09) * mm, v(8.5, -20.15) * mm, v(7.59, -19.07) * mm, v(6.58, -20.65) * mm, v(7.36, -24.98) * mm, v(7.9, -25.42) * mm, v(12.27, -25.42) * mm], "startDerivative": vector(-11.8, 0.95) * mm, "endDerivative": vector(26.49, 0.97) * mm});
            skFitSpline(sketch, "E96", {"points": [v(11.33, -21.31) * mm, v(10.87, -21.98) * mm, v(10.49, -23.06) * mm, v(10.95, -24.07) * mm, v(11.48, -24.63) * mm, v(12.01, -24.35) * mm, v(11.73, -23.35) * mm, v(11.33, -23.62) * mm, v(10.91, -23.01) * mm, v(11.62, -22.12) * mm, v(12.27, -21.75) * mm, v(12.7, -22.46) * mm, v(13.07, -23.5) * mm, v(12.27, -25.42) * mm], "startDerivative": vector(-6.24, -8.5) * mm, "endDerivative": vector(-10.38, -18.2) * mm});
            skFitSpline(sketch, "E97", {"points": [v(12.27, -25.42) * mm, v(13.19, -25.42) * mm], "startDerivative": vector(0.92, 0) * mm, "endDerivative": vector(0.92, 0) * mm});
            skFitSpline(sketch, "E98", {"points": [v(13.19, -25.42) * mm, v(13.39, -25) * mm, v(13.78, -24.06) * mm, v(13.9, -23.5) * mm, v(13.88, -23.27) * mm, v(13.56, -22.58) * mm, v(12.95, -21.4) * mm, v(13.09, -21.24) * mm, v(13.55, -20.68) * mm, v(14.49, -19.46) * mm, v(15.11, -18.48) * mm, v(16.55, -15.56) * mm, v(17.58, -13.2) * mm, v(18.25, -11.48) * mm, v(18.5, -10.15) * mm, v(18.24, -9.7) * mm, v(17.92, -9.37) * mm, v(17.41, -8.67) * mm, v(16.76, -7.68) * mm, v(15.7, -6.21) * mm, v(15.06, -5.42) * mm, v(14.47, -4.73) * mm, v(13.19, -3.36) * mm, v(12.02, -2.31) * mm, v(11.33, -1.77) * mm, v(10.2, -0.88) * mm, v(9.15, -0.1) * mm, v(8.3, 0.49) * mm, v(6.75, 1.42) * mm, v(6.13, 1.7) * mm, v(5.98, 1.77) * mm, v(4.36, 2.3) * mm, v(3.13, 2.7) * mm, v(2.33, 2.96) * mm, v(1.93, 2.76) * mm], "startDerivative": vector(9.02, 18.61) * mm, "endDerivative": vector(-18.86, -14.93) * mm});
            skLineSegment(sketch, "E99", {"start": v(-11.9, -25.42) * mm, "end": v(-11.3, -25.42) * mm});
            skLineSegment(sketch, "E100", {"start": v(6.84, -25.42) * mm, "end": v(7.9, -25.42) * mm});
            skLineSegment(sketch, "E101", {"start": v(-12.65, -15.29) * mm, "end": v(-13.39, -14.8) * mm});
            skSolve(sketch);
        }
        {
            var Q0;
            Q0=makeQuery(id+"F6.imprint","IMPRINT",FACE,{"disambiguationData":[TD([[makeQuery(id+"F6.imprint","IMPRINT",EDGE,{"derivedFrom":sQuery(id+"F6.wireOp",EDGE,"E88")}),-1.0]])]});
            extrude(context, id + "F7", {"entities" : qUnion([Q0]), "operationType" : NewBodyOperationType.ADD, "depth" : 3.17 * mm});
        }
        {
            var Q0;
            Q0=qCreatedBy(makeId("Top.planeOp"),FACE);
            var sketch = newSketch(context, id + "F8", { "sketchPlane" : qUnion([Q0])});
            skLineSegment(sketch, "E102.bottom", {"start": v(40.5, -8.22) * mm, "end": v(-40.5, -8.22) * mm});
            skLineSegment(sketch, "E102.top", {"start": v(40.5, 8.22) * mm, "end": v(-40.5, 8.22) * mm});
            skLineSegment(sketch, "E102.left", {"start": v(40.5, -8.22) * mm, "end": v(40.5, 8.22) * mm});
            skLineSegment(sketch, "E102.right", {"start": v(-40.5, -8.22) * mm, "end": v(-40.5, 8.22) * mm});
            skPoint(sketch, "E102.middle", {"position": v(0, 0) * mm});
            skLineSegment(sketch, "E103", {"start": v(0, -15.84) * mm, "end": v(0, -8.22) * mm});
            skSolve(sketch);
        }
        {
            var Q0;
            Q0=makeQuery(id+"F8.imprint","IMPRINT",FACE,{"disambiguationData":[TD([[makeQuery(id+"F8.imprint","IMPRINT",EDGE,{"derivedFrom":sQuery(id+"F8.wireOp",EDGE,"E102.top")}),1.0]])]});
            extrude(context, id + "F9", {"entities" : qUnion([Q0]), "operationType" : NewBodyOperationType.REMOVE, "oppositeDirection" : true, "depth" : 30.73 * mm, "hasSecondDirection" : true, "secondDirectionOppositeDirection" : false, "secondDirectionDepth" : 25.4 * mm});
        }
        {
            var Q0;
            {var subQ0=sQuery(id+"F0.wireOp",EDGE,"E10");var subQ1=makeQuery(id+"F1.opExtrude","SWEPT_FACE",FACE,{"disambiguationData":[OSD([subQ0])]});var subQ3=sQuery(id+"F0.wireOp",EDGE,"E5");var subQ4=makeQuery(id+"F1.opExtrude","SWEPT_FACE",FACE,{"disambiguationData":[OSD([subQ3])]});var subQ7=sQuery(id+"F4.wireOp",EDGE,"E73");var subQ8=sQuery(id+"F4.wireOp",EDGE,"E48");var subQ9=makeQuery(id+"F1.opExtrude","CAP_EDGE",EDGE,{"disambiguationData":[OSD([subQ0])],"isStart":false});var subQ10=makeQuery(id+"F5.opExtrude","SWEPT_FACE",FACE,{"disambiguationData":[OSD([subQ8]),TDD([makeQuery(id+"F4.imprint","IMPRINT",EDGE,{"disambiguationData":[TD([[makeQuery(id+"F4.imprint","INTERSECT",VERTEX,{"disambiguationData":[OD(1.0)],"derivedFrom":[subQ9,subQ8]}),-1.0]])],"derivedFrom":subQ8})])]});var subQ11=makeQuery(id+"F5.opExtrude","SWEPT_FACE",FACE,{"disambiguationData":[OSD([subQ0])]});var subQ12=sQuery(id+"F0.wireOp",EDGE,"E9");var subQ13=sQuery(id+"F0.wireOp",EDGE,"E6");var subQ14=makeQuery(id+"F1.opExtrude","SWEPT_FACE",FACE,{"disambiguationData":[OSD([subQ13,subQ12])]});var subQ15=sQuery(id+"F0.wireOp",EDGE,"E12");var subQ16=sQuery(id+"F0.wireOp",EDGE,"E11");var subQ17=sQuery(id+"F0.wireOp",EDGE,"E8");var subQ18=sQuery(id+"F0.wireOp",EDGE,"E7");var subQ19=sQuery(id+"F0.wireOp",EDGE,"E4");var subQ20=sQuery(id+"F0.wireOp",EDGE,"E3");var subQ21=sQuery(id+"F0.wireOp",EDGE,"E2");var subQ22=sQuery(id+"F0.wireOp",EDGE,"E1");var subQ23=makeQuery(id+"F1.opExtrude","CAP_FACE",FACE,{"disambiguationData":[OSD([subQ22,subQ21,subQ20,subQ19,subQ3,subQ13,subQ18,subQ17,subQ12,subQ0,subQ16,subQ15])],"isStart":false});var subQ24=makeQuery(id+"F5.opExtrude","SWEPT_FACE",FACE,{"disambiguationData":[OSD([subQ7])]});var subQ28=sQuery(id+"F2.wireOp",EDGE,"E15");var subQ29=makeQuery(id+"F3.opExtrude","SWEPT_FACE",FACE,{"disambiguationData":[OSD([subQ21,subQ28])]});var subQ30=makeQuery(id+"F1.opExtrude","CAP_EDGE",EDGE,{"disambiguationData":[OSD([subQ21])],"isStart":false});var subQ31=makeQuery(id+"F3.opExtrude","SWEPT_FACE",FACE,{"disambiguationData":[OSD([subQ21]),TDD([makeQuery(id+"F2.imprint","IMPRINT",EDGE,{"disambiguationData":[TD([[makeQuery(id+"F2.imprint","INTERSECT",VERTEX,{"disambiguationData":[OD(11.0)],"derivedFrom":[subQ30,subQ28]}),-1.0]])],"derivedFrom":subQ30})])]});var subQ32=makeQuery(id+"F1.opExtrude","SWEPT_FACE",FACE,{"disambiguationData":[OSD([subQ21])]});var subQ33=makeQuery(id+"F1.opExtrude","SWEPT_FACE",FACE,{"disambiguationData":[OSD([subQ19])]});var subQ34=makeQuery(id+"F2.imprint","INTERSECT",VERTEX,{"disambiguationData":[OD(16.0)],"derivedFrom":[subQ30,subQ28]});var subQ35=makeQuery(id+"F3.opExtrude","SWEPT_FACE",FACE,{"disambiguationData":[OSD([subQ21]),TDD([makeQuery(id+"F2.imprint","IMPRINT",EDGE,{"disambiguationData":[TD([[makeQuery(id+"F2.imprint","INTERSECT",VERTEX,{"disambiguationData":[OD(15.0)],"derivedFrom":[subQ30,subQ28]}),-1.0]])],"derivedFrom":subQ30})])]});var subQ36=makeQuery(id+"F3.opExtrude","SWEPT_FACE",FACE,{"disambiguationData":[OSD([subQ21]),TDD([makeQuery(id+"F2.imprint","IMPRINT",EDGE,{"disambiguationData":[TD([[makeQuery(id+"F2.imprint","INTERSECT",VERTEX,{"disambiguationData":[OD(7.0)],"derivedFrom":[subQ30,subQ28]}),-1.0]])],"derivedFrom":subQ30})])]});var subQ37=makeQuery(id+"F3.opExtrude","SWEPT_FACE",FACE,{"disambiguationData":[OSD([subQ21]),TDD([makeQuery(id+"F2.imprint","IMPRINT",EDGE,{"disambiguationData":[TD([[makeQuery(id+"F2.imprint","INTERSECT",VERTEX,{"disambiguationData":[OD(5.0)],"derivedFrom":[subQ30,subQ28]}),-1.0]])],"derivedFrom":subQ30})])]});var subQ38=makeQuery(id+"F3.opExtrude","SWEPT_FACE",FACE,{"disambiguationData":[OSD([subQ21]),TDD([makeQuery(id+"F2.imprint","IMPRINT",EDGE,{"disambiguationData":[TD([[makeQuery(id+"F2.imprint","INTERSECT",VERTEX,{"disambiguationData":[OD(9.0)],"derivedFrom":[subQ30,subQ28]}),-1.0]])],"derivedFrom":subQ30})])]});var subQ39=makeQuery(id+"F3.opExtrude","SWEPT_FACE",FACE,{"disambiguationData":[OSD([subQ21]),TDD([makeQuery(id+"F2.imprint","IMPRINT",EDGE,{"disambiguationData":[TD([[makeQuery(id+"F2.imprint","INTERSECT",VERTEX,{"disambiguationData":[OD(13.0)],"derivedFrom":[subQ30,subQ28]}),-1.0]])],"derivedFrom":subQ30})])]});var subQ40=makeQuery(id+"F1.opExtrude","SWEPT_FACE",FACE,{"disambiguationData":[OSD([subQ20])]});var subQ41=sQuery(id+"F2.wireOp",EDGE,"E13");var subQ42=makeQuery(id+"F3.opExtrude","SWEPT_FACE",FACE,{"disambiguationData":[OSD([subQ28]),TDD([makeQuery(id+"F2.imprint","IMPRINT",EDGE,{"disambiguationData":[TD([[subQ34,-1.0]])],"derivedFrom":subQ28})])]});var subQ45=makeQuery(id+"F3.opExtrude","SWEPT_FACE",FACE,{"disambiguationData":[OSD([subQ21]),TDD([makeQuery(id+"F2.imprint","IMPRINT",EDGE,{"disambiguationData":[TD([[makeQuery(id+"F2.imprint","INTERSECT",VERTEX,{"disambiguationData":[OD(2.0)],"derivedFrom":[subQ30,subQ28]}),1.0]])],"derivedFrom":subQ30})])]});var subQ46=makeQuery(id+"F1.opExtrude","SWEPT_FACE",FACE,{"disambiguationData":[OSD([subQ18])]});var subQ47=makeQuery(id+"F1.opExtrude","SWEPT_FACE",FACE,{"disambiguationData":[OSD([subQ17])]});var subQ48=makeQuery(id+"F3.opExtrude","SWEPT_FACE",FACE,{"disambiguationData":[OSD([subQ41])]});Q0=makeQuery(id+"F7.boolean.opBoolean","SPLIT",FACE,{"disambiguationData":[TD([subQ1])],"derivedFrom":makeQuery(id+"F5.boolean.opBoolean","SPLIT",FACE,{"disambiguationData":[TD([subQ23,subQ32,subQ40,subQ33,subQ4,subQ14,subQ46,subQ47,subQ1,subQ48,subQ29,subQ42,subQ45,subQ37,subQ36,subQ38,subQ31,subQ39,subQ35,subQ10,makeQuery(id+"F5.opExtrude","SWEPT_FACE",FACE,{"disambiguationData":[OSD([sQuery(id+"F4.wireOp",EDGE,"E49")])]}),makeQuery(id+"F5.opExtrude","SWEPT_FACE",FACE,{"disambiguationData":[OSD([sQuery(id+"F4.wireOp",EDGE,"E50")])]}),makeQuery(id+"F5.opExtrude","SWEPT_FACE",FACE,{"disambiguationData":[OSD([sQuery(id+"F4.wireOp",EDGE,"E51")])]}),makeQuery(id+"F5.opExtrude","SWEPT_FACE",FACE,{"disambiguationData":[OSD([sQuery(id+"F4.wireOp",EDGE,"E52")])]}),subQ24,subQ11])],"derivedFrom":makeQuery(id+"F3.boolean.opBoolean","SPLIT",FACE,{"disambiguationData":[TD([subQ40])],"derivedFrom":subQ23})})});}
            var sketch = newSketch(context, id + "F10", { "sketchPlane" : qUnion([Q0])});
            skLineSegment(sketch, "E104", {"start": v(-11.9, -25.5) * mm, "end": v(7.9, -25.5) * mm});
            skLineSegment(sketch, "E105", {"start": v(7.9, -25.5) * mm, "end": v(7.5, -25.2) * mm});
            skLineSegment(sketch, "E106", {"start": v(7.5, -25.2) * mm, "end": v(6.84, -25.42) * mm});
            skLineSegment(sketch, "E107", {"start": v(6.84, -25.42) * mm, "end": v(-11.3, -25.42) * mm});
            skLineSegment(sketch, "E108", {"start": v(-11.3, -25.42) * mm, "end": v(-11.9, -25.42) * mm});
            skSolve(sketch);
        }
        {
            var Q0;
            {var subQ1=sQuery(id+"F10.wireOp",EDGE,"E104");Q0=makeQuery(id+"F10.imprint","IMPRINT",FACE,{"disambiguationData":[TD([[makeQuery(id+"F10.imprint","IMPRINT",EDGE,{"derivedFrom":subQ1}),-1.0]])]});}
            extrude(context, id + "F11", {"entities" : qUnion([Q0]), "operationType" : NewBodyOperationType.ADD, "depth" : 3.17 * mm});
        }
    });
